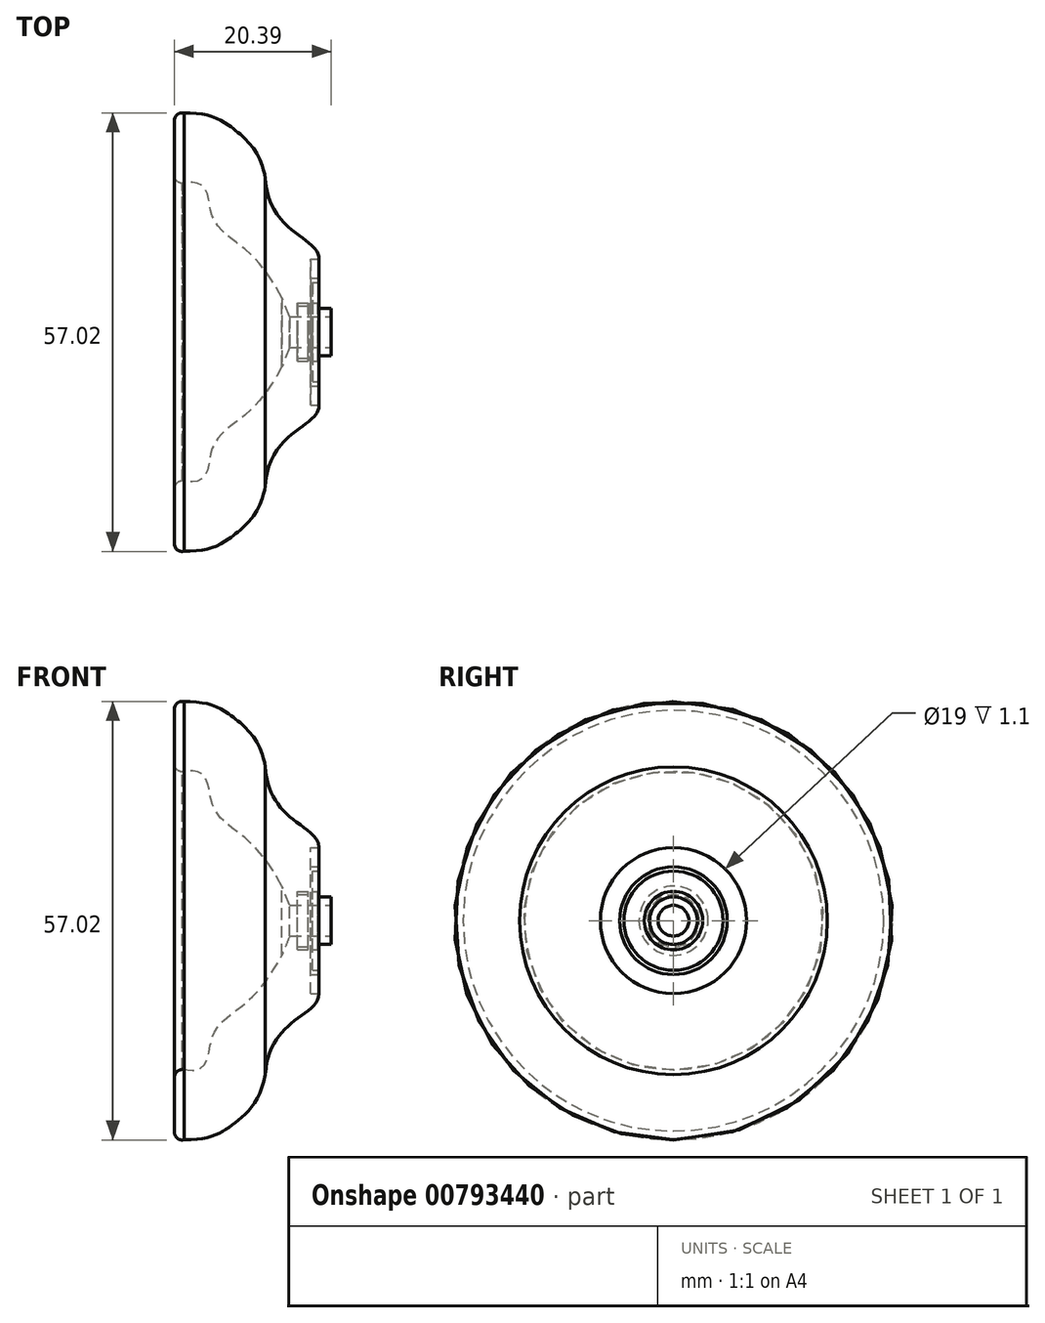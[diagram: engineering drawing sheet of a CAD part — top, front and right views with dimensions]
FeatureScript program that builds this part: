
annotation { "Feature Type Name" : "Feature", "Feature Type Description" : "" }
export const myFeature = defineFeature(function(context is Context, id is Id, definition is map)
    precondition{}
    {
        {
            var Q0;
            Q0=qCreatedBy(makeId("Front.planeOp"),FACE);
            var sketch = newSketch(context, id + "F0", { "sketchPlane" : qUnion([Q0])});
            skLineSegment(sketch, "E0", {"start": v(0, 0) * mm, "end": v(-22, 0) * mm});
            skLineSegment(sketch, "E1", {"start": v(0, 0) * mm, "end": v(0, -10) * mm});
            skLineSegment(sketch, "E2", {"start": v(0, 0) * mm, "end": v(-0.5, 0) * mm});
            skLineSegment(sketch, "E3", {"start": v(-0.5, 0) * mm, "end": v(-0.5, 2) * mm});
            skLineSegment(sketch, "E4", {"start": v(-0.5, 2) * mm, "end": v(-0.5, 3.1) * mm});
            skLineSegment(sketch, "E5", {"start": v(-0.5, 3.1) * mm, "end": v(-2.2, 3.1) * mm});
            skLineSegment(sketch, "E6", {"start": v(-2.2, 3.1) * mm, "end": v(-2.2, 3.8) * mm});
            skLineSegment(sketch, "E7", {"start": v(-2.2, 3.8) * mm, "end": v(-2.9, 3.8) * mm});
            skLineSegment(sketch, "E8", {"start": v(-2.9, 3.8) * mm, "end": v(-2.9, 6.45) * mm});
            skLineSegment(sketch, "E9", {"start": v(-2.9, 6.45) * mm, "end": v(-2.1, 6.45) * mm});
            skLineSegment(sketch, "E10", {"start": v(-2.1, 6.45) * mm, "end": v(-2.1, 7) * mm});
            skLineSegment(sketch, "E11", {"start": v(-2.1, 7) * mm, "end": v(-3.2, 7) * mm});
            skLineSegment(sketch, "E12", {"start": v(-3.2, 7) * mm, "end": v(-3.2, 9.5) * mm});
            skLineSegment(sketch, "E13", {"start": v(-3.2, 9.5) * mm, "end": v(-2.1, 9.5) * mm});
            skPoint(sketch, "E14.visualSharp", {"position": v(-22, 28.5) * mm});
            skArc(sketch, "E14.filletArc", {"start": v(-19.65, 28.49) * mm, "mid": v(-20.57, 28.25) * mm, "end": v(-20.88, 27.35) * mm});
            skLineSegment(sketch, "E15", {"start": v(-2.9, 3.8) * mm, "end": v(-5.9, 3.8) * mm});
            skLineSegment(sketch, "E16", {"start": v(-6.9, 4.5) * mm, "end": v(-5.9, 4.5) * mm});
            skPoint(sketch, "E17.start.orphan", {"position": v(-5.9, 0) * mm});
            skLineSegment(sketch, "E18", {"start": v(-5.9, 4.5) * mm, "end": v(-5.9, 3.8) * mm});
            skLineSegment(sketch, "E19", {"start": v(-20.88, 27.35) * mm, "end": v(-20.88, 20.35) * mm});
            skArc(sketch, "E20.filletArc", {"start": v(-20.88, 20.35) * mm, "mid": v(-20.59, 19.64) * mm, "end": v(-19.88, 19.35) * mm});
            skFitSpline(sketch, "E21", {"points": [v(-19.88, 19.35) * mm, v(-16, 15.2) * mm, v(-11.6, 10.69) * mm, v(-6.9, 4.5) * mm], "startDerivative": vector(36.8, 7.6) * mm, "endDerivative": vector(11.73, -20.91) * mm});
            skLineSegment(sketch, "E22", {"start": v(-0.5, 2) * mm, "end": v(-5.9, 2) * mm});
            skLineSegment(sketch, "E23", {"start": v(-5.9, 2) * mm, "end": v(-6.9, 4.5) * mm});
            skFitSpline(sketch, "E24", {"points": [v(-19.65, 28.49) * mm, v(-13.41, 26.58) * mm, v(-9.06, 20) * mm], "startDerivative": vector(21.83, 0.1) * mm, "endDerivative": vector(4.16, -21.44) * mm});
            skFitSpline(sketch, "E25", {"points": [v(-9.06, 20) * mm, v(-5.26, 13) * mm, v(-2.1, 9.5) * mm], "startDerivative": vector(1.04, -18.97) * mm, "endDerivative": vector(0.1, -10.26) * mm});
            skLineSegment(sketch, "E26", {"start": v(-5.9, 3.8) * mm, "end": v(-4.9, 3.8) * mm});
            skLineSegment(sketch, "E27", {"start": v(-4.9, 3.8) * mm, "end": v(-4.9, 3.38) * mm});
            skLineSegment(sketch, "E28", {"start": v(-4.9, 3.38) * mm, "end": v(-3.5, 3.38) * mm});
            skLineSegment(sketch, "E29", {"start": v(-3.5, 3.38) * mm, "end": v(-3.5, 3.8) * mm});
            skSolve(sketch);
        }
        {
            var Q0;
            Q0 = qSketchRegion(id + "F0", true);
            var Q1;
            Q1=sQuery(id+"F0.wireOp",EDGE,"E0");
            revolve(context, id + "F1", {"surfaceOperationType" : NewSurfaceOperationType.NEW, "entities" : qUnion([Q0]), "axis" : qUnion([Q1]), "revolveType" : RevolveType.FULL});
        }
    });
